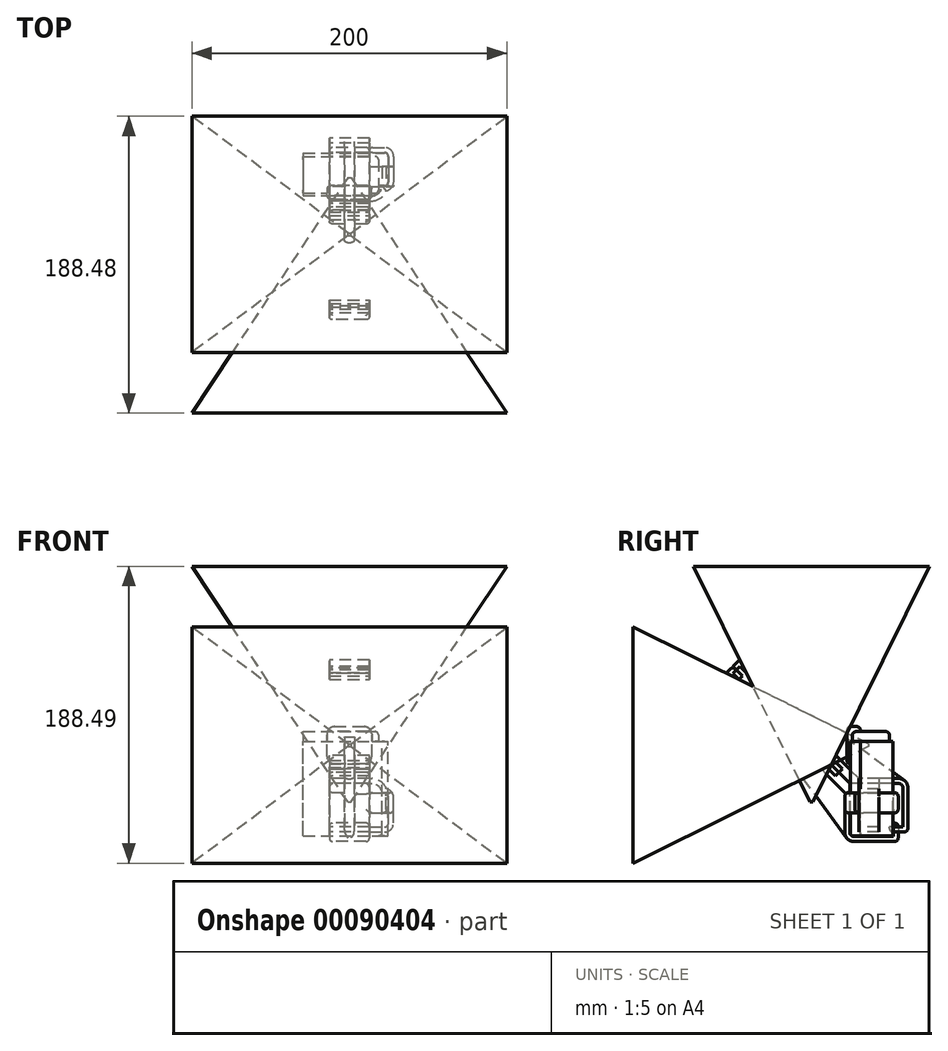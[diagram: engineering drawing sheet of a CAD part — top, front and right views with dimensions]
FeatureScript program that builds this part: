
annotation { "Feature Type Name" : "Feature", "Feature Type Description" : "" }
export const myFeature = defineFeature(function(context is Context, id is Id, definition is map)
    precondition{}
    {
        {
            var Q0;
            Q0=qCreatedBy(makeId("Top.planeOp"),FACE);
            var sketch = newSketch(context, id + "F0", { "sketchPlane" : qUnion([Q0])});
            skLineSegment(sketch, "E0.bottom", {"start": v(-14.25, 0) * mm, "end": v(14.25, 0) * mm, "construction": true});
            skLineSegment(sketch, "E0.top", {"start": v(-14.25, -20) * mm, "end": v(14.25, -20) * mm, "construction": true});
            skLineSegment(sketch, "E0.left", {"start": v(-14.25, 0) * mm, "end": v(-14.25, -20) * mm, "construction": true});
            skLineSegment(sketch, "E0.right", {"start": v(14.25, 0) * mm, "end": v(14.25, -20) * mm, "construction": true});
            skPoint(sketch, "E1", {"position": v(0, 0) * mm});
            skLineSegment(sketch, "E2.bottom", {"start": v(-29.4, 9.15) * mm, "end": v(20.6, 9.15) * mm, "construction": true});
            skLineSegment(sketch, "E2.top", {"start": v(-29.4, -17.85) * mm, "end": v(20.6, -17.85) * mm, "construction": true});
            skLineSegment(sketch, "E2.left", {"start": v(-29.4, 9.15) * mm, "end": v(-29.4, -17.85) * mm, "construction": true});
            skLineSegment(sketch, "E2.right", {"start": v(20.6, 9.15) * mm, "end": v(20.6, -17.85) * mm, "construction": true});
            skPoint(sketch, "E3", {"position": v(14.25, -17.85) * mm});
            skArc(sketch, "E4", {"start": v(14.25, -17.85) * mm, "mid": v(18.74, -16) * mm, "end": v(20.6, -11.5) * mm});
            skLineSegment(sketch, "E5", {"start": v(20.6, -11.5) * mm, "end": v(20.6, 9.15) * mm});
            skLineSegment(sketch, "E6", {"start": v(-29.4, 9.15) * mm, "end": v(20.6, 9.15) * mm});
            skLineSegment(sketch, "E7", {"start": v(-29.4, 9.15) * mm, "end": v(-29.4, -17.85) * mm});
            skLineSegment(sketch, "E8", {"start": v(-29.4, -17.85) * mm, "end": v(14.25, -17.85) * mm});
            skLineSegment(sketch, "E9", {"start": v(20.6, 9.15) * mm, "end": v(22.45, 9.15) * mm});
            skLineSegment(sketch, "E10", {"start": v(24.6, 7) * mm, "end": v(24.6, -9.35) * mm});
            skLineSegment(sketch, "E11", {"start": v(22.45, -11.5) * mm, "end": v(20.6, -11.5) * mm});
            skPoint(sketch, "E12.visualSharp", {"position": v(24.6, 9.15) * mm});
            skArc(sketch, "E12.filletArc", {"start": v(24.6, 7) * mm, "mid": v(23.97, 8.52) * mm, "end": v(22.45, 9.15) * mm});
            skPoint(sketch, "E13.visualSharp", {"position": v(24.6, -11.5) * mm});
            skArc(sketch, "E13.filletArc", {"start": v(22.45, -11.5) * mm, "mid": v(23.97, -10.88) * mm, "end": v(24.6, -9.35) * mm});
            skSolve(sketch);
        }
        {
            var Q0;
            Q0=makeQuery(id+"F0.imprint","IMPRINT",FACE,{"disambiguationData":[TD([[makeQuery(id+"F0.imprint","IMPRINT",EDGE,{"derivedFrom":sQuery(id+"F0.wireOp",EDGE,"E4")}),1.0]])]});
            var Q1;
            Q1=makeQuery(id+"F0.imprint","IMPRINT",FACE,{"disambiguationData":[TD([[makeQuery(id+"F0.imprint","IMPRINT",EDGE,{"derivedFrom":sQuery(id+"F0.wireOp",EDGE,"E5")}),-1.0]])]});
            extrude(context, id + "F1", {"entities" : qUnion([Q0, Q1]), "oppositeDirection" : true, "depth" : 60 * mm});
        }
        {
            var Q0;
            Q0=makeQuery(id+"F1.opExtrude","SWEPT_FACE",FACE,{"disambiguationData":[OSD([sQuery(id+"F0.wireOp",EDGE,"E8")])]});
            var sketch = newSketch(context, id + "F2", { "sketchPlane" : qUnion([Q0])});
            skLineSegment(sketch, "E14.bottom", {"start": v(-9.49, 9.52) * mm, "end": v(9.49, 9.52) * mm});
            skLineSegment(sketch, "E14.top", {"start": v(-9.49, -13.98) * mm, "end": v(9.49, -13.98) * mm});
            skLineSegment(sketch, "E14.left", {"start": v(-14.25, 4.76) * mm, "end": v(-14.25, -9.21) * mm});
            skLineSegment(sketch, "E14.right", {"start": v(14.25, 4.76) * mm, "end": v(14.25, -9.21) * mm});
            skPoint(sketch, "E15", {"position": v(-14.25, 0) * mm});
            skPoint(sketch, "E16.visualSharp", {"position": v(-14.25, 9.52) * mm});
            skArc(sketch, "E16.filletArc", {"start": v(-9.49, 9.53) * mm, "mid": v(-12.86, 8.13) * mm, "end": v(-14.25, 4.76) * mm});
            skPoint(sketch, "E17.visualSharp", {"position": v(14.25, 9.52) * mm});
            skArc(sketch, "E17.filletArc", {"start": v(14.25, 4.76) * mm, "mid": v(12.86, 8.13) * mm, "end": v(9.49, 9.52) * mm});
            skPoint(sketch, "E18.visualSharp", {"position": v(14.25, -13.98) * mm});
            skArc(sketch, "E18.filletArc", {"start": v(9.49, -13.98) * mm, "mid": v(12.86, -12.58) * mm, "end": v(14.25, -9.21) * mm});
            skPoint(sketch, "E19.visualSharp", {"position": v(-14.25, -13.98) * mm});
            skArc(sketch, "E19.filletArc", {"start": v(-14.25, -9.21) * mm, "mid": v(-12.86, -12.58) * mm, "end": v(-9.49, -13.97) * mm});
            skSolve(sketch);
        }
        {
            var Q0;
            Q0 = qSketchRegion(id + "F2", true);
            extrude(context, id + "F3", {"entities" : qUnion([Q0]), "operationType" : NewBodyOperationType.ADD, "depth" : (8.5 - 6.35) * mm, "hasSecondDirection" : true, "secondDirectionOppositeDirection" : true, "secondDirectionDepth" : 6.35 * mm});
        }
        {
            var Q0;
            Q0=makeQuery(id+"F1.opExtrude","CAP_FACE",FACE,{"disambiguationData":[OSD([sQuery(id+"F0.wireOp",EDGE,"E4"),sQuery(id+"F0.wireOp",EDGE,"E5"),sQuery(id+"F0.wireOp",EDGE,"E6"),sQuery(id+"F0.wireOp",EDGE,"E7"),sQuery(id+"F0.wireOp",EDGE,"E8")])],"isStart":true});
            var sketch = newSketch(context, id + "F4", { "sketchPlane" : qUnion([Q0])});
            skLineSegment(sketch, "E20.bottom", {"start": v(-29.4, 7) * mm, "end": v(16.3, 7) * mm});
            skLineSegment(sketch, "E20.top", {"start": v(-29.4, -16.44) * mm, "end": v(16.3, -16.44) * mm});
            skLineSegment(sketch, "E20.left", {"start": v(-29.4, 7) * mm, "end": v(-29.4, -16.44) * mm});
            skLineSegment(sketch, "E20.right", {"start": v(18.45, 4.85) * mm, "end": v(18.45, -14.3) * mm});
            skPoint(sketch, "E21.visualSharp", {"position": v(18.45, 7) * mm});
            skArc(sketch, "E21.filletArc", {"start": v(18.45, 4.85) * mm, "mid": v(17.82, 6.37) * mm, "end": v(16.3, 7) * mm});
            skPoint(sketch, "E22.visualSharp", {"position": v(18.45, -16.44) * mm});
            skArc(sketch, "E22.filletArc", {"start": v(16.3, -16.44) * mm, "mid": v(17.82, -15.81) * mm, "end": v(18.45, -14.3) * mm});
            skSolve(sketch);
        }
        {
            var Q0;
            Q0 = qSketchRegion(id + "F4", true);
            extrude(context, id + "F5", {"entities" : qUnion([Q0]), "operationType" : NewBodyOperationType.ADD, "depth" : 6.35 * mm});
        }
        {
            var Q0;
            Q0=makeQuery(id+"F5.opExtrude","CAP_EDGE",EDGE,{"disambiguationData":[OSD([sQuery(id+"F4.wireOp",EDGE,"E20.bottom")])],"isStart":false});
            var Q1;
            {var subQ0=sQuery(id+"F4.wireOp",EDGE,"E20.top");Q1=makeQuery(id+"F5.boolean.opBoolean","SPLIT",EDGE,{"disambiguationData":[TD([makeQuery(id+"F1.opExtrude","SWEPT_FACE",FACE,{"disambiguationData":[OSD([sQuery(id+"F0.wireOp",EDGE,"E7")])]})])],"derivedFrom":makeQuery(id+"F5.opExtrude","CAP_EDGE",EDGE,{"disambiguationData":[OSD([subQ0])],"isStart":false})});}
            var Q2;
            Q2=makeQuery(id+"F3.opExtrude","CAP_EDGE",EDGE,{"disambiguationData":[OSD([sQuery(id+"F2.wireOp",EDGE,"E14.left")])],"isStart":false});
            var Q3;
            Q3=makeQuery(id+"F1.opExtrude","CAP_EDGE",EDGE,{"disambiguationData":[OSD([sQuery(id+"F0.wireOp",EDGE,"E8")])],"isStart":false});
            var Q4;
            Q4=makeQuery(id+"F3.opExtrude","CAP_EDGE",EDGE,{"disambiguationData":[OSD([sQuery(id+"F2.wireOp",EDGE,"E14.bottom")])],"isStart":true});
            fillet(context, id + "F6", {"entities" : qUnion([Q0, Q1, Q2, Q3, Q4]), "radius" : (8.5 - 6.35) * mm, "tangentPropagation" : true, "allowEdgeOverflow" : false});
        }
        {
            var Q0;
            Q0=qCreatedBy(makeId("Front.planeOp"),FACE);
            cPlane(context, id + "F7", {"entities" : qUnion([Q0]), "cplaneType" : CPlaneType.OFFSET, "offset" : 6.35 * mm, "width" : 150 * mm, "height" : 150 * mm});
        }
        {
            var Q0;
            Q0=qCreatedBy(id+"F7.planeOp",FACE);
            var sketch = newSketch(context, id + "F8", { "sketchPlane" : qUnion([Q0])});
            skPoint(sketch, "E23.5", {"position": v(-14.25, 9.52) * mm});
            skPoint(sketch, "E23.7", {"position": v(14.25, 9.52) * mm});
            skPoint(sketch, "E23.9", {"position": v(14.25, -13.98) * mm});
            skPoint(sketch, "E23.11", {"position": v(-14.25, -13.98) * mm});
            skLineSegment(sketch, "E24", {"start": v(-14.25, 9.52) * mm, "end": v(14.25, -13.98) * mm, "construction": true});
            skLineSegment(sketch, "E25", {"start": v(14.25, 9.52) * mm, "end": v(-14.25, -13.98) * mm, "construction": true});
            skPoint(sketch, "E26", {"position": v(0, -2.23) * mm});
            skLineSegment(sketch, "E27.bottom", {"start": v(-1, -1.4) * mm, "end": v(1, -1.4) * mm});
            skLineSegment(sketch, "E27.top", {"start": v(-1, -3.05) * mm, "end": v(1, -3.05) * mm});
            skLineSegment(sketch, "E27.left", {"start": v(-1, -1.4) * mm, "end": v(-1, -3.05) * mm});
            skLineSegment(sketch, "E27.right", {"start": v(1, -1.4) * mm, "end": v(1, -3.05) * mm});
            skSolve(sketch);
        }
        {
            var Q0;
            Q0=qCreatedBy(makeId("Front.planeOp"),FACE);
            cPlane(context, id + "F9", {"entities" : qUnion([Q0]), "cplaneType" : CPlaneType.OFFSET, "offset" : 156 * mm, "width" : 150 * mm, "height" : 150 * mm});
        }
        {
            var Q0;
            Q0=qCreatedBy(id+"F9.planeOp",FACE);
            var sketch = newSketch(context, id + "F10", { "sketchPlane" : qUnion([Q0])});
            skPoint(sketch, "E28.0", {"position": v(0, -2.23) * mm});
            skLineSegment(sketch, "E29.bottom", {"start": v(-100, 72.78) * mm, "end": v(100, 72.78) * mm});
            skLineSegment(sketch, "E29.top", {"start": v(-100, -77.22) * mm, "end": v(100, -77.22) * mm});
            skLineSegment(sketch, "E29.left", {"start": v(-100, 72.78) * mm, "end": v(-100, -77.22) * mm});
            skLineSegment(sketch, "E29.right", {"start": v(100, 72.78) * mm, "end": v(100, -77.22) * mm});
            skLineSegment(sketch, "E30", {"start": v(-100, 72.77) * mm, "end": v(100, -77.23) * mm, "construction": true});
            skLineSegment(sketch, "E31", {"start": v(-100, -77.22) * mm, "end": v(100, 72.77) * mm, "construction": true});
            skSolve(sketch);
        }
        {
            var Q1;
            Q1 = qSketchRegion(id + "F8", true);
            var Q2;
            Q2=makeQuery(id+"F10.imprint","IMPRINT",FACE,{"disambiguationData":[TD([[makeQuery(id+"F10.imprint","IMPRINT",EDGE,{"derivedFrom":sQuery(id+"F10.wireOp",EDGE,"E29.bottom")}),-1.0]])]});
            loft(context, id + "F11", {"sheetProfilesArray" : [{ "sheetProfileEntities" : qUnion([Q1]) }, { "sheetProfileEntities" : qUnion([Q2]) }]});
        }
        {
            var Q0;
            Q0=qCreatedBy(makeId("Right.planeOp"),FACE);
            var sketch = newSketch(context, id + "F12", { "sketchPlane" : qUnion([Q0])});
            skLineSegment(sketch, "E32.0", {"start": v(-18.1, -57.85) * mm, "end": v(-18.1, -26.64) * mm});
            skArc(sketch, "E32.1", {"start": v(-18.1, -57.85) * mm, "mid": v(-17.4, -59.55) * mm, "end": v(-15.7, -60.25) * mm});
            skLineSegment(sketch, "E32.2", {"start": v(-11.5, -60.25) * mm, "end": v(-15.7, -60.25) * mm});
            skLineSegment(sketch, "E32.3", {"start": v(9.15, -60.25) * mm, "end": v(-11.5, -60.25) * mm});
            skLineSegment(sketch, "E33.0", {"start": v(-21.28, -57.85) * mm, "end": v(-21.28, -32.45) * mm});
            skArc(sketch, "E33.1", {"start": v(-21.28, -57.85) * mm, "mid": v(-19.64, -61.8) * mm, "end": v(-15.7, -63.42) * mm});
            skLineSegment(sketch, "E33.2", {"start": v(-11.5, -63.42) * mm, "end": v(-15.7, -63.42) * mm});
            skLineSegment(sketch, "E33.3", {"start": v(9.15, -63.42) * mm, "end": v(-11.5, -63.42) * mm});
            skLineSegment(sketch, "E34", {"start": v(9.15, -60.25) * mm, "end": v(9.4, -60.25) * mm});
            skLineSegment(sketch, "E35", {"start": v(9.4, -60.25) * mm, "end": v(9.4, -51.75) * mm});
            skLineSegment(sketch, "E36", {"start": v(10.42, -51.75) * mm, "end": v(9.4, -51.75) * mm});
            skLineSegment(sketch, "E37", {"start": v(12.57, -53.9) * mm, "end": v(12.57, -61.27) * mm});
            skLineSegment(sketch, "E38", {"start": v(9.15, -63.42) * mm, "end": v(10.42, -63.42) * mm});
            skPoint(sketch, "E39.visualSharp", {"position": v(12.57, -51.75) * mm});
            skArc(sketch, "E39.filletArc", {"start": v(12.57, -53.9) * mm, "mid": v(11.95, -52.38) * mm, "end": v(10.42, -51.75) * mm});
            skPoint(sketch, "E40.visualSharp", {"position": v(12.57, -63.42) * mm});
            skArc(sketch, "E40.filletArc", {"start": v(10.42, -63.42) * mm, "mid": v(11.95, -62.8) * mm, "end": v(12.57, -61.27) * mm});
            skLineSegment(sketch, "E41", {"start": v(-21.27, -32.45) * mm, "end": v(-96.96, 43.24) * mm});
            skLineSegment(sketch, "E42", {"start": v(-96.96, 43.24) * mm, "end": v(-92.47, 47.73) * mm});
            skLineSegment(sketch, "E43", {"start": v(-92.47, 47.73) * mm, "end": v(-18.1, -26.64) * mm, "construction": true});
            skLineSegment(sketch, "E44", {"start": v(-90.22, 45.48) * mm, "end": v(-92.47, 43.24) * mm});
            skPoint(sketch, "E44.startSnap0", {"position": v(-94.72, 45.48) * mm});
            skLineSegment(sketch, "E45", {"start": v(-92.47, 43.24) * mm, "end": v(-27.42, -21.82) * mm});
            skLineSegment(sketch, "E46", {"start": v(-27.42, -21.82) * mm, "end": v(-25.17, -19.57) * mm});
            skLineSegment(sketch, "E47", {"start": v(-25.17, -19.57) * mm, "end": v(-18.1, -26.64) * mm});
            skLineSegment(sketch, "E48", {"start": v(-27.42, -26.3) * mm, "end": v(-22.93, -21.82) * mm});
            skLineSegment(sketch, "E49", {"start": v(-92.47, 47.73) * mm, "end": v(-90.22, 45.48) * mm});
            skLineSegment(sketch, "E50", {"start": v(-96.96, 43.24) * mm, "end": v(-19.64, -61.9) * mm});
            skPoint(sketch, "E50.endSnap0", {"position": v(-19.64, -61.8) * mm});
            skSolve(sketch);
        }
        {
            var Q0;
            {var subQ4=sQuery(id+"F12.wireOp",EDGE,"E32.0");Q0=makeQuery(id+"F12.imprint","IMPRINT",FACE,{"disambiguationData":[TD([[makeQuery(id+"F12.imprint","IMPRINT",EDGE,{"derivedFrom":subQ4}),1.0]])]});}
            var Q1;
            {var subQ0=sQuery(id+"F12.wireOp",EDGE,"E42");Q1=makeQuery(id+"F12.imprint","IMPRINT",FACE,{"disambiguationData":[TD([[makeQuery(id+"F12.imprint","IMPRINT",EDGE,{"derivedFrom":subQ0}),-1.0]])]});}
            extrude(context, id + "F13", {"entities" : qUnion([Q0, Q1]), "depth" : 12.7 * mm, "hasSecondDirection" : true, "secondDirectionOppositeDirection" : true, "secondDirectionDepth" : 12.7 * mm});
        }
        {
            var Q0;
            Q0=makeQuery(id+"F13.opExtrude","SWEPT_EDGE",EDGE,{"disambiguationData":[OSD([sQuery(id+"F12.wireOp",EDGE,"E33.0"),sQuery(id+"F12.wireOp",EDGE,"E41")])]});
            var Q1;
            Q1=makeQuery(id+"F1.opExtrude","CAP_EDGE",EDGE,{"disambiguationData":[OSD([sQuery(id+"F0.wireOp",EDGE,"E10")])],"isStart":false});
            cPlane(context, id + "F14", {"entities" : qUnion([Q0, Q1]), "cplaneType" : CPlaneType.LINE_ANGLE, "offset" : 150 * mm, "angle" : 0 * degree, "width" : 150 * mm, "height" : 150 * mm});
        }
        {
            var Q0;
            Q0=qCreatedBy(id+"F14.planeOp",FACE);
            var sketch = newSketch(context, id + "F15", { "sketchPlane" : qUnion([Q0])});
            skArc(sketch, "E51.0", {"start": v(14.25, -17.85) * mm, "mid": v(18.74, -16) * mm, "end": v(20.6, -11.5) * mm, "construction": true});
            skLineSegment(sketch, "E51.1", {"start": v(12.7, -17.85) * mm, "end": v(14.25, -17.85) * mm, "construction": true});
            skLineSegment(sketch, "E51.2", {"start": v(22.45, -11.5) * mm, "end": v(20.6, -11.5) * mm, "construction": true});
            skArc(sketch, "E51.3", {"start": v(22.45, -11.5) * mm, "mid": v(23.97, -10.88) * mm, "end": v(24.6, -9.35) * mm, "construction": true});
            skLineSegment(sketch, "E51.4", {"start": v(24.6, 7) * mm, "end": v(24.6, -9.35) * mm, "construction": true});
            skArc(sketch, "E51.5", {"start": v(24.6, 7) * mm, "mid": v(23.97, 8.52) * mm, "end": v(22.45, 9.15) * mm, "construction": true});
            skLineSegment(sketch, "E51.6", {"start": v(12.7, 9.15) * mm, "end": v(22.45, 9.15) * mm, "construction": true});
            skPoint(sketch, "E52.orphan", {"position": v(12.7, 10.42) * mm});
            skPoint(sketch, "E53.orphan", {"position": v(12.7, -21.28) * mm});
            skLineSegment(sketch, "E54.0", {"start": v(12.7, 9.4) * mm, "end": v(22.45, 9.4) * mm});
            skArc(sketch, "E54.1", {"start": v(24.85, 7) * mm, "mid": v(24.15, 8.7) * mm, "end": v(22.45, 9.4) * mm});
            skLineSegment(sketch, "E54.2", {"start": v(24.85, 7) * mm, "end": v(24.85, -9.35) * mm});
            skLineSegment(sketch, "E54.3", {"start": v(12.7, -18.1) * mm, "end": v(14.25, -18.1) * mm});
            skArc(sketch, "E54.4", {"start": v(14.25, -18.1) * mm, "mid": v(18.83, -16.26) * mm, "end": v(20.85, -11.75) * mm});
            skLineSegment(sketch, "E54.5", {"start": v(22.45, -11.75) * mm, "end": v(20.85, -11.75) * mm});
            skArc(sketch, "E54.6", {"start": v(22.45, -11.75) * mm, "mid": v(24.15, -11.05) * mm, "end": v(24.85, -9.35) * mm});
            skLineSegment(sketch, "E55.0", {"start": v(12.7, 12.57) * mm, "end": v(22.45, 12.57) * mm});
            skArc(sketch, "E55.1", {"start": v(28.03, 7) * mm, "mid": v(26.4, 10.94) * mm, "end": v(22.45, 12.57) * mm});
            skLineSegment(sketch, "E55.2", {"start": v(12.7, -21.28) * mm, "end": v(14.25, -21.28) * mm});
            skArc(sketch, "E55.3", {"start": v(14.25, -21.28) * mm, "mid": v(19.86, -19.5) * mm, "end": v(23.44, -14.84) * mm});
            skArc(sketch, "E55.4", {"start": v(23.44, -14.84) * mm, "mid": v(26.73, -12.93) * mm, "end": v(28.03, -9.35) * mm});
            skLineSegment(sketch, "E55.5", {"start": v(28.02, 7) * mm, "end": v(28.02, -9.35) * mm});
            skLineSegment(sketch, "E56", {"start": v(12.7, -21.28) * mm, "end": v(12.7, -18.1) * mm});
            skLineSegment(sketch, "E57", {"start": v(12.7, 12.57) * mm, "end": v(12.7, 9.4) * mm});
            skSolve(sketch);
        }
        {
            var Q0;
            Q0=makeQuery(id+"F15.imprint","IMPRINT",FACE,{"disambiguationData":[TD([[makeQuery(id+"F15.imprint","IMPRINT",EDGE,{"derivedFrom":sQuery(id+"F15.wireOp",EDGE,"E54.0")}),1.0]])]});
            extrude(context, id + "F16", {"entities" : qUnion([Q0]), "operationType" : NewBodyOperationType.ADD, "oppositeDirection" : true, "depth" : 12.7 * mm});
        }
        {
            var Q0;
            {var subQ4=sQuery(id+"F12.wireOp",EDGE,"E33.0");Q0=makeQuery(id+"F12.imprint","IMPRINT",FACE,{"disambiguationData":[TD([[makeQuery(id+"F12.imprint","IMPRINT",EDGE,{"derivedFrom":subQ4}),1.0]])]});}
            extrude(context, id + "F17", {"entities" : qUnion([Q0]), "operationType" : NewBodyOperationType.ADD, "depth" : (6.35 / 2) * mm, "hasSecondDirection" : true, "secondDirectionOppositeDirection" : true, "secondDirectionDepth" : (6.35 / 2) * mm});
        }
        {
            var Q0;
            Q0=makeQuery(id+"F11.opLoft","SWEPT_BODY",BODY,{"disambiguationData":[OSD([makeQuery(id+"F8.imprint","IMPRINT",FACE,{"disambiguationData":[TD([[makeQuery(id+"F8.imprint","IMPRINT",EDGE,{"derivedFrom":sQuery(id+"F8.wireOp",EDGE,"E27.bottom")}),-1.0]])]}),makeQuery(id+"F10.imprint","IMPRINT",FACE,{"disambiguationData":[TD([[makeQuery(id+"F10.imprint","IMPRINT",EDGE,{"derivedFrom":sQuery(id+"F10.wireOp",EDGE,"E29.bottom")}),-1.0]])]})])]});
            var Q1;
            {var subQ0=sQuery(id+"F12.wireOp",EDGE,"E47");Q1=makeQuery(id+"F5WdupdNTrScFfJ_2.boolean.opBoolean","MERGE",FACE,{"derivedFrom":[makeQuery(id+"F13.opExtrude","SWEPT_FACE",FACE,{"disambiguationData":[OSD([subQ0])]}),makeQuery(id+"F5WdupdNTrScFfJ_2.opExtrude","SWEPT_FACE",FACE,{"disambiguationData":[OSD([subQ0])]})]});}
            mirror(context, id + "F18", {"entities" : qUnion([Q0]), "mirrorPlane" : qUnion([Q1])});
        }
        {
            var Q0;
            Q0=makeQuery(id+"F13.opExtrude","SWEPT_FACE",FACE,{"disambiguationData":[OSD([sQuery(id+"F12.wireOp",EDGE,"E45")])]});
            extrude(context, id + "F19", {"entities" : qUnion([Q0]), "depth" : (6.35 / 2) * mm});
        }
        {
            var Q0;
            Q0=makeQuery(id+"F13.opExtrude","CAP_EDGE",EDGE,{"disambiguationData":[OSD([sQuery(id+"F12.wireOp",EDGE,"E33.1")])],"isStart":true});
            var Q1;
            Q1=makeQuery(id+"F13.opExtrude","CAP_EDGE",EDGE,{"disambiguationData":[OSD([sQuery(id+"F12.wireOp",EDGE,"E33.1")])],"isStart":false});
            var Q2;
            Q2=makeQuery(id+"F13.opExtrude","CAP_EDGE",EDGE,{"disambiguationData":[OSD([sQuery(id+"F12.wireOp",EDGE,"E47")])],"isStart":false});
            var Q3;
            Q3=makeQuery(id+"F13.opExtrude","CAP_EDGE",EDGE,{"disambiguationData":[OSD([sQuery(id+"F12.wireOp",EDGE,"E47")])],"isStart":true});
            var Q4;
            Q4=makeQuery(id+"F13.opExtrude","CAP_EDGE",EDGE,{"disambiguationData":[OSD([sQuery(id+"F12.wireOp",EDGE,"E41")])],"isStart":true});
            var Q5;
            Q5=makeQuery(id+"F13.opExtrude","CAP_EDGE",EDGE,{"disambiguationData":[OSD([sQuery(id+"F12.wireOp",EDGE,"E41")])],"isStart":false});
            var Q6;
            Q6=makeQuery(id+"F17.opExtrude","CAP_EDGE",EDGE,{"disambiguationData":[OSD([sQuery(id+"F12.wireOp",EDGE,"E50")])],"isStart":true});
            var Q7;
            Q7=makeQuery(id+"F17.opExtrude","CAP_EDGE",EDGE,{"disambiguationData":[OSD([sQuery(id+"F12.wireOp",EDGE,"E50")])],"isStart":false});
            var Q8;
            Q8=makeQuery(id+"F16.opExtrude","CAP_EDGE",EDGE,{"disambiguationData":[OSD([sQuery(id+"F15.wireOp",EDGE,"E55.1")])],"isStart":false});
            var Q9;
            Q9=makeQuery(id+"F16.opExtrude","CAP_EDGE",EDGE,{"disambiguationData":[OSD([sQuery(id+"F15.wireOp",EDGE,"E55.1")])],"isStart":true});
            var Q10;
            Q10=makeQuery(id+"F16.opExtrude","CAP_EDGE",EDGE,{"disambiguationData":[OSD([sQuery(id+"F15.wireOp",EDGE,"E55.3")])],"isStart":false});
            var Q11;
            Q11=makeQuery(id+"F16.opExtrude","CAP_EDGE",EDGE,{"disambiguationData":[OSD([sQuery(id+"F15.wireOp",EDGE,"E55.3")])],"isStart":true});
            var Q12;
            Q12=makeQuery(id+"F16.opExtrude","SWEPT_FACE",FACE,{"disambiguationData":[OSD([sQuery(id+"F15.wireOp",EDGE,"E55.0")])]});
            var Q13;
            Q13=makeQuery(id+"F16.opExtrude","CAP_EDGE",EDGE,{"disambiguationData":[OSD([sQuery(id+"F15.wireOp",EDGE,"E57")])],"isStart":false});
            var Q14;
            Q14=makeQuery(id+"F16.opExtrude","CAP_EDGE",EDGE,{"disambiguationData":[OSD([sQuery(id+"F15.wireOp",EDGE,"E57")])],"isStart":true});
            fillet(context, id + "F20", {"entities" : qUnion([Q0, Q1, Q2, Q3, Q4, Q5, Q6, Q7, Q8, Q9, Q10, Q11, Q12, Q13, Q14]), "radius" : (8.5 - 6.35) * mm, "tangentPropagation" : true, "allowEdgeOverflow" : false});
        }
        {
            var Q0;
            Q0=makeQuery(id+"F13.opExtrude","SWEPT_EDGE",EDGE,{"disambiguationData":[OSD([sQuery(id+"F12.wireOp",EDGE,"E42"),sQuery(id+"F12.wireOp",EDGE,"E49")])]});
            var Q1;
            {var subQ0=sQuery(id+"F12.wireOp",EDGE,"E50");var subQ1=sQuery(id+"F12.wireOp",EDGE,"E41");var subQ2=sQuery(id+"F12.wireOp",EDGE,"E33.1");var subQ3=sQuery(id+"F12.wireOp",EDGE,"E33.0");var subQ4=sQuery(id+"F12.wireOp",EDGE,"E42");Q1=makeQuery(id+"F17.boolean.opBoolean","SPLIT",EDGE,{"disambiguationData":[TD([makeQuery(id+"F17.opExtrude","CAP_FACE",FACE,{"disambiguationData":[OSD([subQ3,subQ2,subQ1,subQ0])],"isStart":true})])],"derivedFrom":makeQuery(id+"F13.opExtrude","SWEPT_EDGE",EDGE,{"disambiguationData":[OSD([subQ1,subQ4,subQ0])]})});}
            var Q2;
            {var subQ0=sQuery(id+"F12.wireOp",EDGE,"E50");var subQ1=sQuery(id+"F12.wireOp",EDGE,"E41");var subQ2=sQuery(id+"F12.wireOp",EDGE,"E33.1");var subQ3=sQuery(id+"F12.wireOp",EDGE,"E33.0");var subQ4=sQuery(id+"F12.wireOp",EDGE,"E42");Q2=makeQuery(id+"F17.boolean.opBoolean","SPLIT",EDGE,{"disambiguationData":[TD([makeQuery(id+"F17.opExtrude","CAP_FACE",FACE,{"disambiguationData":[OSD([subQ3,subQ2,subQ1,subQ0])],"isStart":false})])],"derivedFrom":makeQuery(id+"F13.opExtrude","SWEPT_EDGE",EDGE,{"disambiguationData":[OSD([subQ1,subQ4,subQ0])]})});}
            var Q3;
            Q3=makeQuery(id+"F13.opExtrude","CAP_EDGE",EDGE,{"disambiguationData":[OSD([sQuery(id+"F12.wireOp",EDGE,"E42")])],"isStart":false});
            var Q4;
            Q4=makeQuery(id+"F13.opExtrude","CAP_EDGE",EDGE,{"disambiguationData":[OSD([sQuery(id+"F12.wireOp",EDGE,"E42")])],"isStart":true});
            fillet(context, id + "F21", {"entities" : qUnion([Q0, Q1, Q2, Q3, Q4]), "radius" : (8.5 - 6.35) * mm, "allowEdgeOverflow" : false});
        }
    });
